# Revit family: Providence Small
name_source: partatom
category: Lighting Fixtures
units: mm (PartAtom-declared; Revit-internal decimal feet)

## family parameters
Cut with Voids When Loaded = No
Host = Face
Light Source = No
OmniClass Number = 23.80.70.14
OmniClass Title = Luminaries for External Lighting
Part Type = Normal
Room Calculation Point = No
Round Connector Dimension = Use Diameter
Shared = No

## types (13) — shared parameters
Apparent Load = 0 VA
Default Elevation = 48.000"
Description = PROS-Providence Small
Lamp = LED Lamp
Light Bulb Material = Glass-Frosted
Load Classification = Lighting
Manufacturer = Architectural Area Lighting
Model = PROS
URL = https://www.currentlighting.com
Wattage Comments = 25-82W

## per-type parameters (varying)
| type | Finish | Photometric web | Pole Height |
| Arctic White | Aluminum-Artic White | Web Pros : PROS-27LED-BW | 144.000" |
| Black | Aluminum-Black | Web Pros : PROS-27LED-BW | 144.000" |
| Matte Black | Aluminum-Matte Black | Web Pros : PROS-27LED-BW | 144.000" |
| Dark Green | Aluminum-Dark Green | Web Pros : PROS-27LED-BW | 144.000" |
| Dark Bronze | Aluminum-Dark Bronze | Web Pros : PROS-27LED-BW | 144.000" |
| Wheathered Bronze | Aluminum-Weathered Bronze | Web Pros : PROS-27LED-BW | 100.000" |
| Metallic Bronze | Aluminum-Metalic Bronze | Web Pros : PROS-27LED-BW | 144.000" |
| Verde Blue | Aluminum-Verde Blue | Web Pros : PROS-27LED-BW | 144.000" |
| Corten | Aluminum-Corten | Web Pros : PROS-27LED-BW | 144.000" |
| Matte Aluminum | Aluminum-Matte | Web Pros : PROS-27LED-BW | 144.000" |
| Medium Grey | Aluminum-Medium Grey | Web Pros : PROS-27LED-BW | 144.000" |
| Antique Green | Aluminum-Antique Green | Web Pros : PROS-Y3-2040-HTD | 144.000" |
| Light Grey | Aluminum-Light Grey | Web Pros : PROS-27LED-BW | 144.000" |

## geometry (parser evidence)
native form markers: Blend x32, Sweep x9
no freeform markers — native parametric forms only
